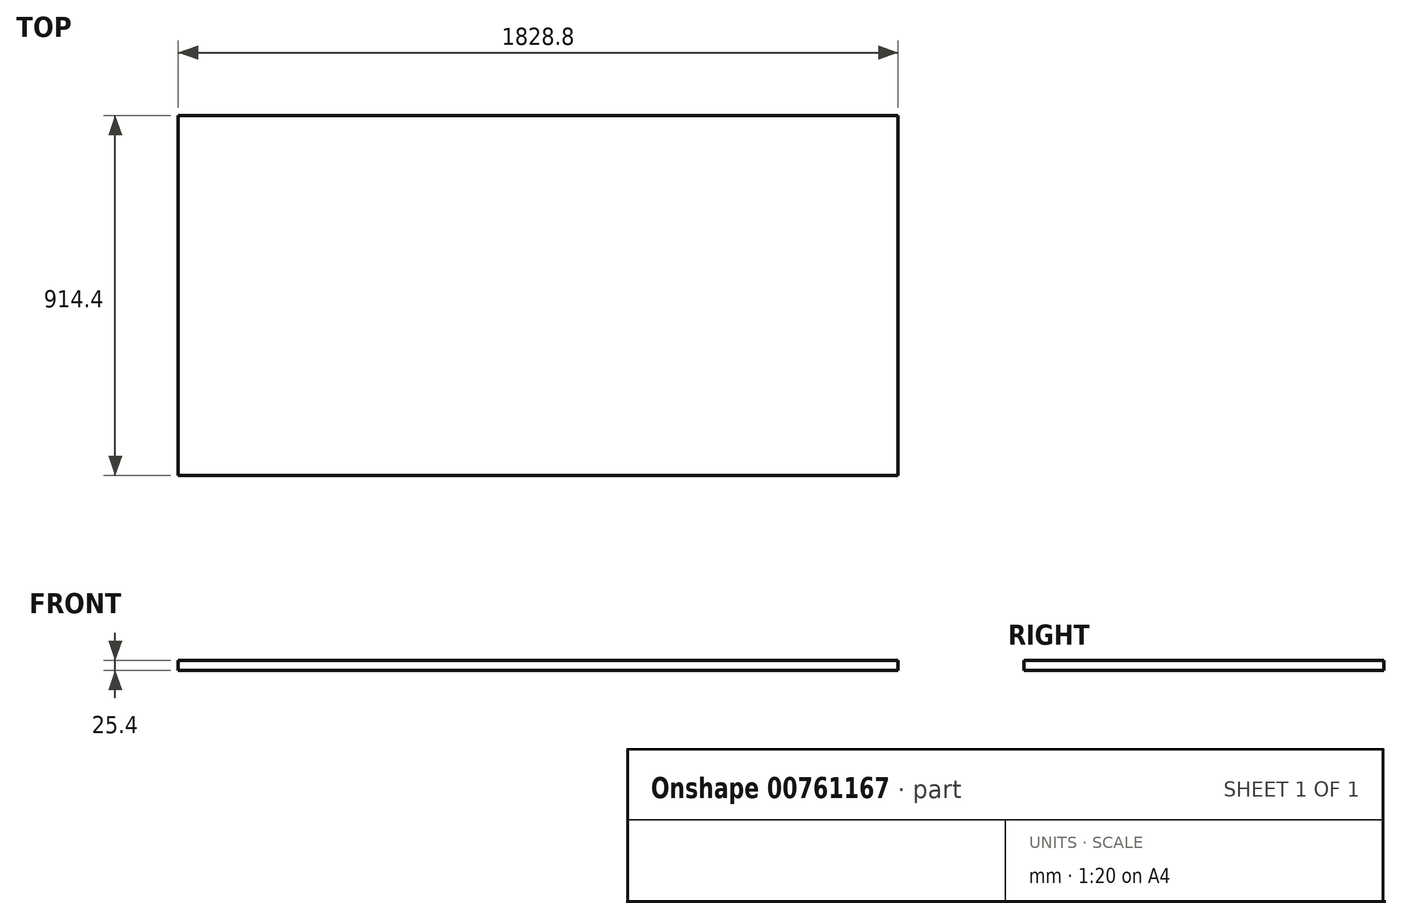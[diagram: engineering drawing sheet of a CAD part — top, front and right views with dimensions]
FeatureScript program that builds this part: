
annotation { "Feature Type Name" : "Feature", "Feature Type Description" : "" }
export const myFeature = defineFeature(function(context is Context, id is Id, definition is map)
    precondition{}
    {
        {
            var Q0;
            Q0=qCreatedBy(makeId("Top.planeOp"),FACE);
            var sketch = newSketch(context, id + "F0", { "sketchPlane" : qUnion([Q0])});
            skLineSegment(sketch, "E0", {"start": v(-487.1, 470.52) * mm, "end": v(1341.7, 470.52) * mm});
            skLineSegment(sketch, "E1", {"start": v(1341.7, 470.52) * mm, "end": v(1341.7, -443.88) * mm});
            skLineSegment(sketch, "E2", {"start": v(1341.7, -443.88) * mm, "end": v(-487.1, -443.88) * mm});
            skLineSegment(sketch, "E3", {"start": v(-487.1, -443.88) * mm, "end": v(-487.1, 470.52) * mm});
            skSolve(sketch);
        }
        {
            var Q0;
            Q0 = qSketchRegion(id + "F0", true);
            extrude(context, id + "F1", {"entities" : qUnion([Q0]), "depth" : 25.4 * mm, "offsetDistance" : 25.4 * mm});
        }
    });
